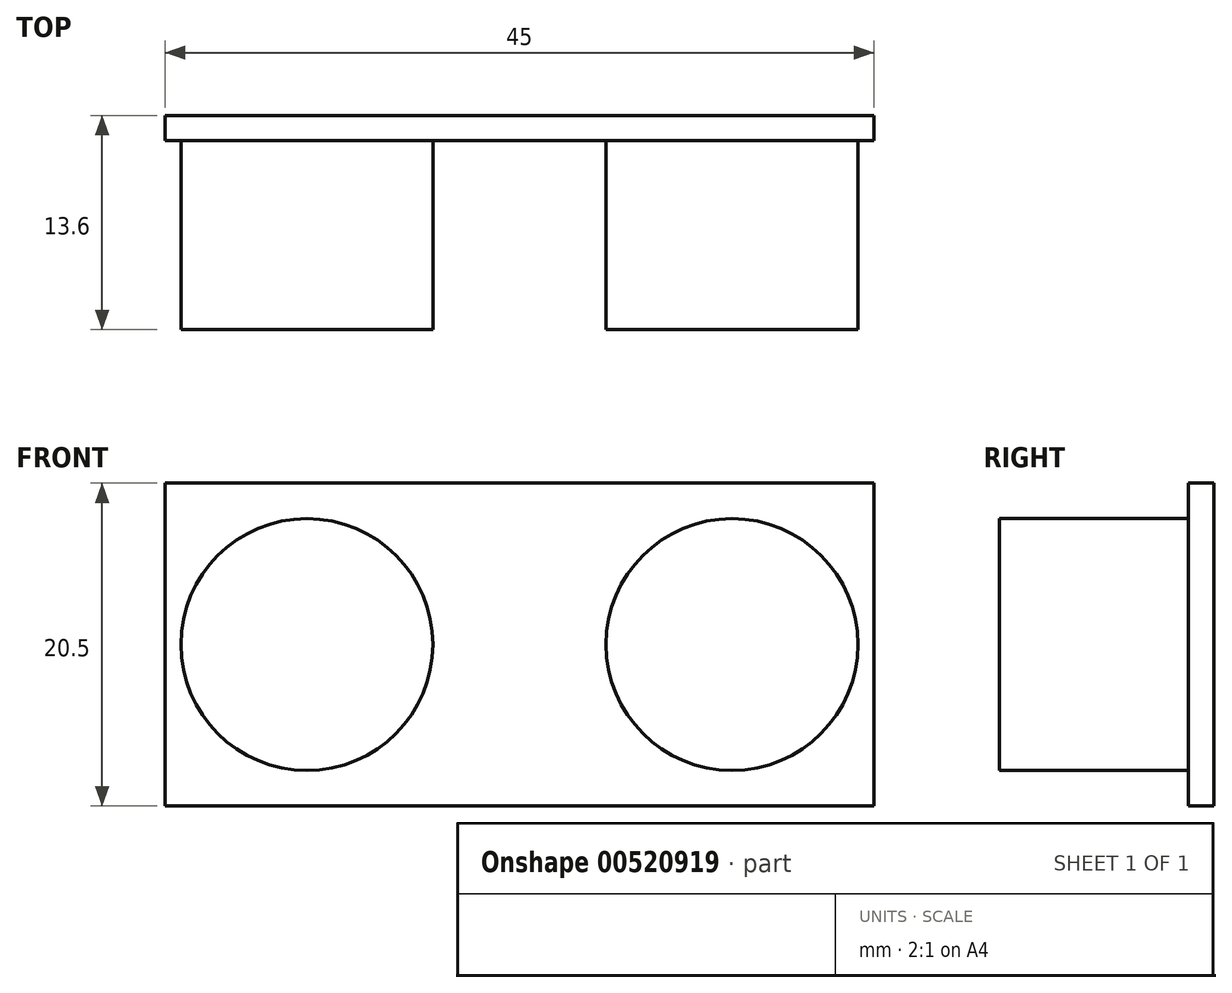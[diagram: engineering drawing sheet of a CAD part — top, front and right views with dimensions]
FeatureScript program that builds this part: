
annotation { "Feature Type Name" : "Feature", "Feature Type Description" : "" }
export const myFeature = defineFeature(function(context is Context, id is Id, definition is map)
    precondition{}
    {
        {
            var Q0;
            Q0=qCreatedBy(makeId("Front.planeOp"),FACE);
            var sketch = newSketch(context, id + "F0", { "sketchPlane" : qUnion([Q0])});
            skLineSegment(sketch, "E0.bottom", {"start": v(22.5, -8.8) * mm, "end": v(-22.5, -8.8) * mm});
            skLineSegment(sketch, "E0.top", {"start": v(22.5, 11.7) * mm, "end": v(-22.5, 11.7) * mm});
            skLineSegment(sketch, "E0.left", {"start": v(22.5, -8.8) * mm, "end": v(22.5, 11.7) * mm});
            skLineSegment(sketch, "E0.right", {"start": v(-22.5, -8.8) * mm, "end": v(-22.5, 11.7) * mm});
            skPoint(sketch, "E0.middle", {"position": v(0, 1.45) * mm});
            skSolve(sketch);
        }
        {
            var Q0;
            Q0 = qSketchRegion(id + "F0", true);
            extrude(context, id + "F1", {"entities" : qUnion([Q0]), "depth" : 1.6 * mm, "offsetDistance" : 25.4 * mm});
        }
        {
            var Q0;
            Q0=makeQuery(id+"F1.opExtrude","CAP_FACE",FACE,{"disambiguationData":[OSD([sQuery(id+"F0.wireOp",EDGE,"E0.bottom"),sQuery(id+"F0.wireOp",EDGE,"E0.top"),sQuery(id+"F0.wireOp",EDGE,"E0.left"),sQuery(id+"F0.wireOp",EDGE,"E0.right")])],"isStart":false});
            var sketch = newSketch(context, id + "F2", { "sketchPlane" : qUnion([Q0])});
            skCircle(sketch, "E1", {"center": v(-13.5, 1.45) * mm, "radius": 8 * mm});
            skCircle(sketch, "E2", {"center": v(13.5, 1.45) * mm, "radius": 8 * mm});
            skLineSegment(sketch, "E3", {"start": v(0, 11.7) * mm, "end": v(0, -8.8) * mm});
            skLineSegment(sketch, "E4", {"start": v(-5.5, 1.45) * mm, "end": v(5.5, 1.45) * mm});
            skPoint(sketch, "E5", {"position": v(0, 1.45) * mm});
            skPoint(sketch, "E5.positionSnap0", {"position": v(0, 1.45) * mm});
            skSolve(sketch);
        }
        {
            var Q0;
            Q0 = qSketchRegion(id + "F2", true);
            extrude(context, id + "F3", {"entities" : qUnion([Q0]), "operationType" : NewBodyOperationType.ADD, "depth" : 12 * mm, "offsetDistance" : 25.4 * mm});
        }
    });
